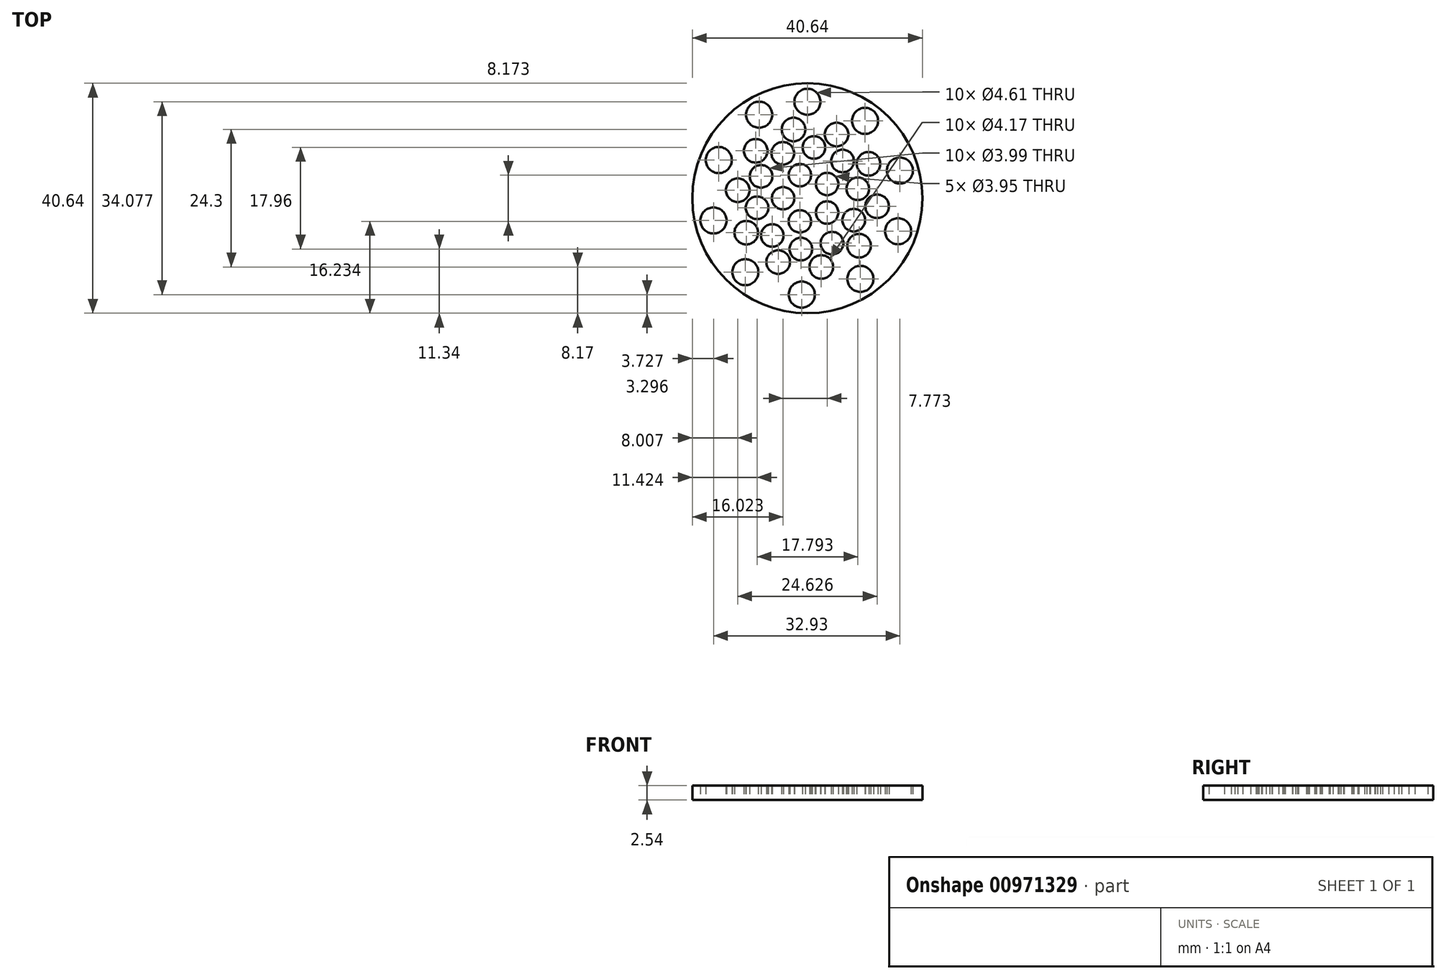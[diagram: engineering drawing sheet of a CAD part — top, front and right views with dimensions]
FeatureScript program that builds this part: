
annotation { "Feature Type Name" : "Feature", "Feature Type Description" : "" }
export const myFeature = defineFeature(function(context is Context, id is Id, definition is map)
    precondition{}
    {
        {
            var Q0;
            Q0=qCreatedBy(makeId("Top.planeOp"),FACE);
            var sketch = newSketch(context, id + "F0", { "sketchPlane" : qUnion([Q0])});
            skCircle(sketch, "E0", {"center": v(0, 0) * mm, "radius": 20.32 * mm});
            skCircle(sketch, "E1", {"center": v(0, 17.05) * mm, "radius": 2.3 * mm});
            skCircle(sketch, "E2.1.0", {"center": v(10.18, 13.68) * mm, "radius": 2.3 * mm});
            skCircle(sketch, "E2.2.0", {"center": v(16.34, 4.9) * mm, "radius": 2.3 * mm});
            skCircle(sketch, "E2.3.0", {"center": v(16.02, -5.83) * mm, "radius": 2.3 * mm});
            skCircle(sketch, "E2.4.0", {"center": v(9.37, -14.25) * mm, "radius": 2.3 * mm});
            skCircle(sketch, "E2.5.0", {"center": v(-1, -17.02) * mm, "radius": 2.3 * mm});
            skCircle(sketch, "E2.6.0", {"center": v(-10.96, -13.06) * mm, "radius": 2.3 * mm});
            skCircle(sketch, "E2.7.0", {"center": v(-16.6, -3.93) * mm, "radius": 2.3 * mm});
            skCircle(sketch, "E2.8.0", {"center": v(-15.66, 6.75) * mm, "radius": 2.3 * mm});
            skCircle(sketch, "E2.9.0", {"center": v(-8.53, 14.77) * mm, "radius": 2.3 * mm});
            skLineSegment(sketch, "E2.anchor1", {"start": v(0, 0) * mm, "end": v(0, 17.05) * mm, "construction": true});
            skLineSegment(sketch, "E2.anchor2", {"start": v(0, 0) * mm, "end": v(-8.53, 14.77) * mm, "construction": true});
            skCircle(sketch, "E3", {"center": v(-9.13, 8.39) * mm, "radius": 2.09 * mm});
            skCircle(sketch, "E4.1.0", {"center": v(-12.31, 1.42) * mm, "radius": 2.09 * mm});
            skCircle(sketch, "E4.2.0", {"center": v(-10.8, -6.09) * mm, "radius": 2.09 * mm});
            skCircle(sketch, "E4.3.0", {"center": v(-5.16, -11.27) * mm, "radius": 2.09 * mm});
            skCircle(sketch, "E4.4.0", {"center": v(2.45, -12.15) * mm, "radius": 2.09 * mm});
            skCircle(sketch, "E4.5.0", {"center": v(9.13, -8.39) * mm, "radius": 2.09 * mm});
            skCircle(sketch, "E4.6.0", {"center": v(12.31, -1.42) * mm, "radius": 2.09 * mm});
            skCircle(sketch, "E4.7.0", {"center": v(10.8, 6.09) * mm, "radius": 2.09 * mm});
            skCircle(sketch, "E4.8.0", {"center": v(5.16, 11.27) * mm, "radius": 2.09 * mm});
            skCircle(sketch, "E5.1.9.0", {"center": v(-2.45, 12.15) * mm, "radius": 2.09 * mm});
            skCircle(sketch, "E6", {"center": v(-8.18, 3.87) * mm, "radius": 2 * mm});
            skCircle(sketch, "E7.1.0", {"center": v(-8.9, -1.68) * mm, "radius": 2 * mm});
            skCircle(sketch, "E7.2.0", {"center": v(-6.2, -6.59) * mm, "radius": 2 * mm});
            skCircle(sketch, "E7.3.0", {"center": v(-1.15, -8.98) * mm, "radius": 2 * mm});
            skCircle(sketch, "E7.4.0", {"center": v(4.35, -7.94) * mm, "radius": 2 * mm});
            skCircle(sketch, "E7.5.0", {"center": v(8.18, -3.87) * mm, "radius": 2 * mm});
            skCircle(sketch, "E7.6.0", {"center": v(8.9, 1.68) * mm, "radius": 2 * mm});
            skCircle(sketch, "E7.7.0", {"center": v(6.2, 6.59) * mm, "radius": 2 * mm});
            skCircle(sketch, "E7.8.0", {"center": v(1.15, 8.98) * mm, "radius": 2 * mm});
            skCircle(sketch, "E7.9.0", {"center": v(-4.35, 7.94) * mm, "radius": 2 * mm});
            skCircle(sketch, "E8", {"center": v(-4.3, 0) * mm, "radius": 1.98 * mm});
            skCircle(sketch, "E9.1.0", {"center": v(-1.33, -4.09) * mm, "radius": 1.98 * mm});
            skCircle(sketch, "E9.2.0", {"center": v(3.48, -2.53) * mm, "radius": 1.98 * mm});
            skCircle(sketch, "E9.3.0", {"center": v(3.48, 2.53) * mm, "radius": 1.98 * mm});
            skCircle(sketch, "E9.4.0", {"center": v(-1.33, 4.09) * mm, "radius": 1.98 * mm});
            skSolve(sketch);
        }
        {
            var Q0;
            Q0=makeQuery(id+"F0.imprint","IMPRINT",FACE,{"disambiguationData":[TD([[makeQuery(id+"F0.imprint","IMPRINT",EDGE,{"derivedFrom":sQuery(id+"F0.wireOp",EDGE,"E0")}),1.0]])]});
            extrude(context, id + "F1", {"entities" : qUnion([Q0]), "depth" : 2.54 * mm, "offsetDistance" : 25.4 * mm});
        }
    });
